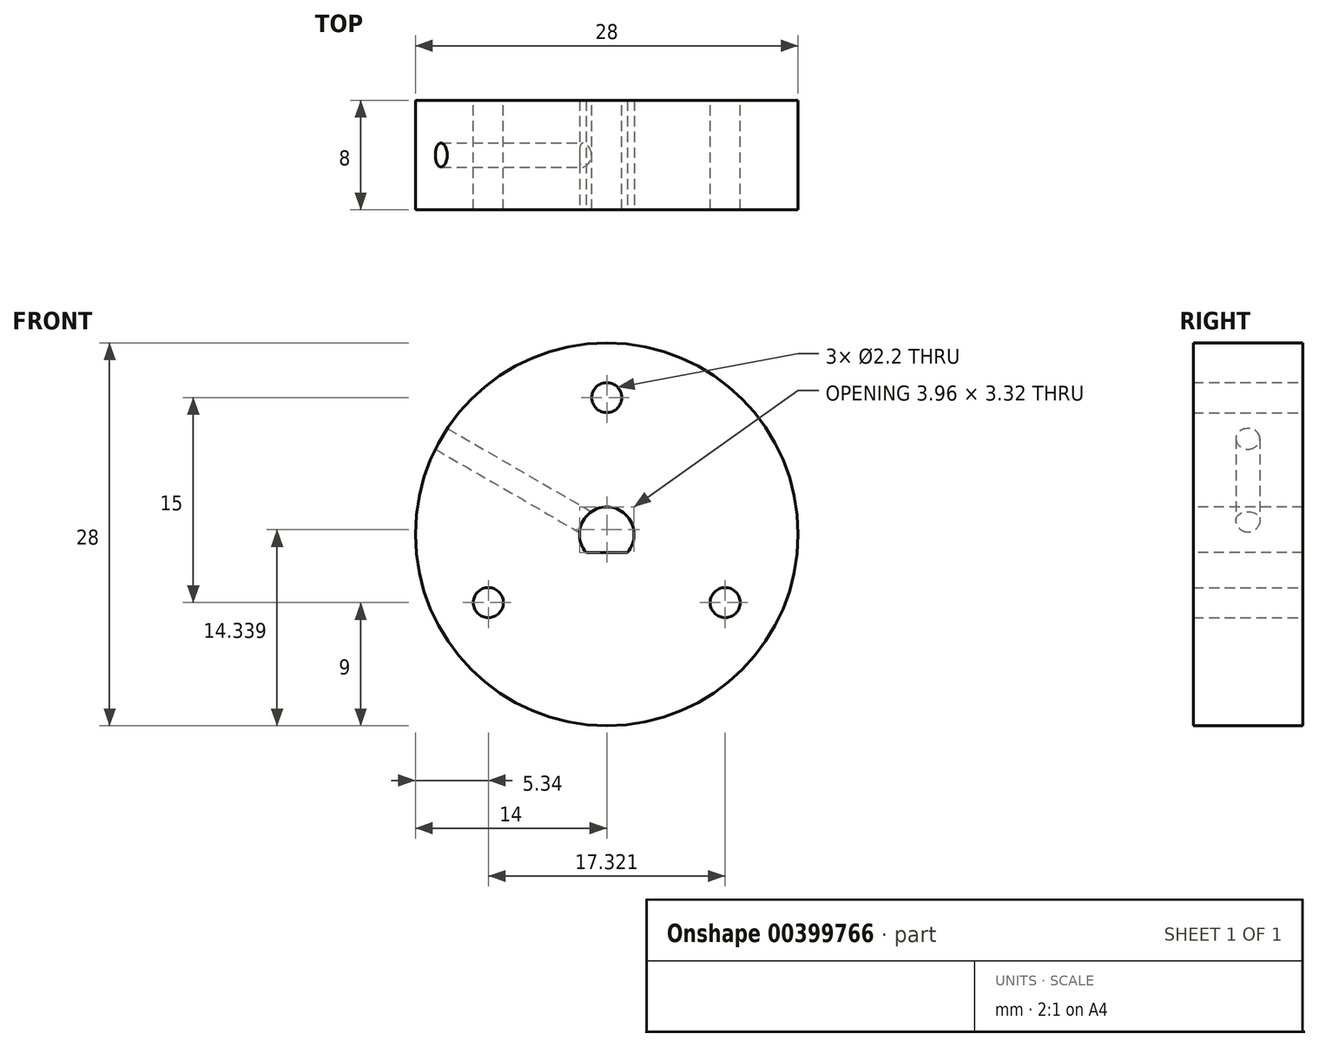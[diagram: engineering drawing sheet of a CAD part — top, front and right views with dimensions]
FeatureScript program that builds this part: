
annotation { "Feature Type Name" : "Feature", "Feature Type Description" : "" }
export const myFeature = defineFeature(function(context is Context, id is Id, definition is map)
    precondition{}
    {
        {
            var Q0;
            Q0=qCreatedBy(makeId("Front.planeOp"),FACE);
            var sketch = newSketch(context, id + "F0", { "sketchPlane" : qUnion([Q0])});
            skCircle(sketch, "E0", {"center": v(0, 0) * mm, "radius": 10 * mm, "construction": true});
            skLineSegment(sketch, "E1.0", {"start": v(0, 10) * mm, "end": v(8.66, -5) * mm, "construction": true});
            skLineSegment(sketch, "E1.1", {"start": v(8.66, -5) * mm, "end": v(-8.66, -5) * mm, "construction": true});
            skLineSegment(sketch, "E1.2", {"start": v(-8.66, -5) * mm, "end": v(0, 10) * mm, "construction": true});
            skCircle(sketch, "E2", {"center": v(0, 10) * mm, "radius": 1.1 * mm});
            skCircle(sketch, "E3", {"center": v(8.66, -5) * mm, "radius": 1.1 * mm});
            skCircle(sketch, "E4", {"center": v(-8.66, -5) * mm, "radius": 1.1 * mm});
            skCircle(sketch, "E5", {"center": v(0, 0) * mm, "radius": 14 * mm});
            skSolve(sketch);
        }
        {
            var Q0;
            Q0=makeQuery(id+"F0.imprint","IMPRINT",FACE,{"disambiguationData":[TD([[makeQuery(id+"F0.imprint","IMPRINT",EDGE,{"derivedFrom":sQuery(id+"F0.wireOp",EDGE,"E2")}),-1.0]])]});
            extrude(context, id + "F1", {"entities" : qUnion([Q0]), "depth" : 8 * mm});
        }
        {
            var Q0;
            Q0=makeQuery(id+"F1.opExtrude","CAP_FACE",FACE,{"disambiguationData":[OSD([sQuery(id+"F0.wireOp",EDGE,"E2"),sQuery(id+"F0.wireOp",EDGE,"E3"),sQuery(id+"F0.wireOp",EDGE,"E4"),sQuery(id+"F0.wireOp",EDGE,"E5")])],"isStart":false});
            var sketch = newSketch(context, id + "F2", { "sketchPlane" : qUnion([Q0])});
            skArc(sketch, "E6", {"start": v(1.5, -1.32) * mm, "mid": v(0, 2) * mm, "end": v(-1.5, -1.32) * mm});
            skLineSegment(sketch, "E7.bottom", {"start": v(1.5, -1.32) * mm, "end": v(-1.5, -1.32) * mm});
            skPoint(sketch, "E7.top.end.orphan", {"position": v(-1.5, 1.32) * mm});
            skPoint(sketch, "E7.left.end.orphan", {"position": v(1.5, 1.32) * mm});
            skSolve(sketch);
        }
        {
            var Q0;
            Q0=qSketchRegion(id+"F2",true);
            extrude(context, id + "F3", {"entities" : qUnion([Q0]), "operationType" : NewBodyOperationType.REMOVE, "endBound" : BoundingType.THROUGH_ALL, "oppositeDirection" : true, "depth" : 25 * mm});
        }
        {
            var Q0;
            Q0=qCreatedBy(makeId("Right.planeOp"),FACE);
            var sketch = newSketch(context, id + "F4", { "sketchPlane" : qUnion([Q0])});
            skLineSegment(sketch, "E8", {"start": v(32.06, 0) * mm, "end": v(-30.06, 0) * mm, "construction": true});
            skSolve(sketch);
        }
        {
            var Q0;
            Q0=sQuery(id+"F4.wireOp",EDGE,"E8");
            cPlane(context, id + "F5", {"entities" : qUnion([Q0]), "cplaneType" : CPlaneType.LINE_ANGLE, "offset" : 25 * mm, "angle" : 60 * degree, "width" : 150 * mm, "height" : 150 * mm});
        }
        {
            var Q0;
            Q0=qCreatedBy(id+"F5.planeOp",FACE);
            var sketch = newSketch(context, id + "F6", { "sketchPlane" : qUnion([Q0])});
            skCircle(sketch, "E9", {"center": v(-4, 0) * mm, "radius": 0.88 * mm});
            skSolve(sketch);
        }
        {
            var Q0;
            Q0=qSketchRegion(id+"F6",true);
            extrude(context, id + "F7", {"entities" : qUnion([Q0]), "operationType" : NewBodyOperationType.REMOVE, "endBound" : BoundingType.THROUGH_ALL, "oppositeDirection" : true, "depth" : 25 * mm});
        }
    });
